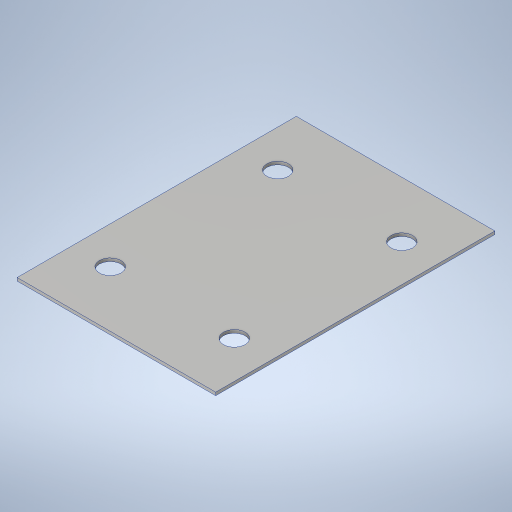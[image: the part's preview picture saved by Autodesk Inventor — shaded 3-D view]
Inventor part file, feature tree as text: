
AUTODESK INVENTOR PART (.ipt)
format: ipt  version: 2023.4 (Build 274418000, 418)  size: 224,768 bytes
history: native  units: in
note: dims shown in document units (in); Inventor stores cm internally (conversion verified against a paired STEP export)
features: sketch x2, extrude x1, hole x1
ambient origin geometry x8: Origin, YZ Plane, XZ Plane, XY Plane, X Axis, Y Axis, Z Axis, Center Point
bodies: Solid1 (feature_tree)
feature tree (4):
  extrude  "Extrusion1"  Depth=11.25in
  hole  "Hole1"  [1 undecoded]
  sketch  "Sketch1"  dims[d0=8.0in d1=11.25in]
  sketch  "Sketch2"  dims[d2=0.125in d3=0.0in d4=3.375in d5=2.5in d6=0.875in d7=0.328in d8=0.375in d9=0.25in d10=0.5635in d11=1.0in d12=0.8108in]
note: 1 required parameter value undecoded (feature->parameter linkage not recoverable at this tier; creation-order binding heuristic only, values carry confidence <= 0.55)
